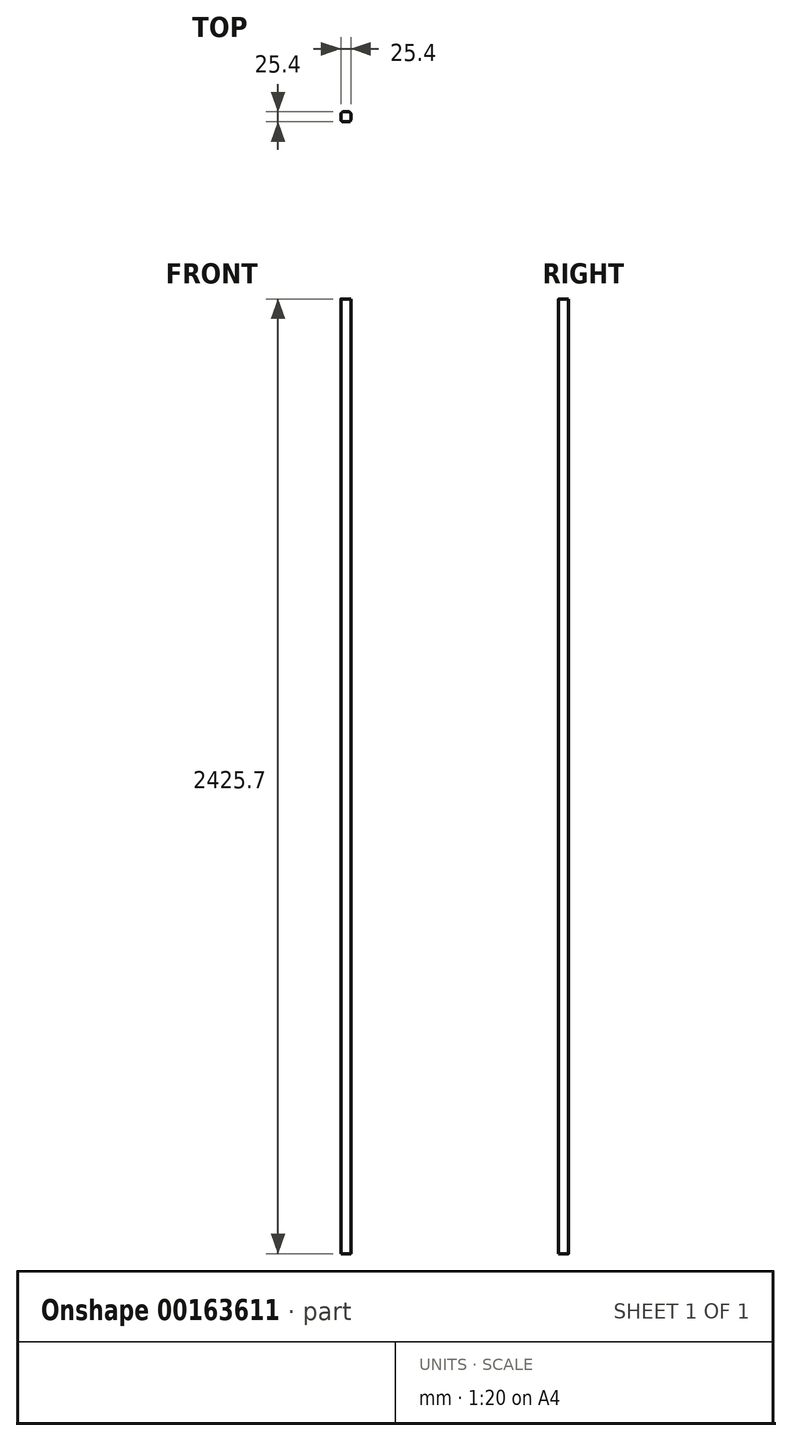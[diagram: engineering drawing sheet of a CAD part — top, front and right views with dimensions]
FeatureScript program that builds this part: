
annotation { "Feature Type Name" : "Feature", "Feature Type Description" : "" }
export const myFeature = defineFeature(function(context is Context, id is Id, definition is map)
    precondition{}
    {
        {
            var Q0;
            Q0=qCreatedBy(makeId("Top.planeOp"),FACE);
            var sketch = newSketch(context, id + "F0", { "sketchPlane" : qUnion([Q0])});
            skLineSegment(sketch, "E0.bottom", {"start": v(6.35, 12.7) * mm, "end": v(-6.35, 12.7) * mm});
            skLineSegment(sketch, "E0.top", {"start": v(6.35, -12.7) * mm, "end": v(-6.35, -12.7) * mm});
            skLineSegment(sketch, "E0.left", {"start": v(12.7, 6.35) * mm, "end": v(12.7, -6.35) * mm});
            skLineSegment(sketch, "E0.right", {"start": v(-12.7, 6.35) * mm, "end": v(-12.7, -6.35) * mm});
            skPoint(sketch, "E0.middle", {"position": v(0, 0) * mm});
            skPoint(sketch, "E1.visualSharp", {"position": v(-12.7, 12.7) * mm});
            skArc(sketch, "E1.filletArc", {"start": v(-6.35, 12.7) * mm, "mid": v(-10.84, 10.84) * mm, "end": v(-12.7, 6.35) * mm});
            skPoint(sketch, "E2.visualSharp", {"position": v(12.7, 12.7) * mm});
            skArc(sketch, "E2.filletArc", {"start": v(12.7, 6.35) * mm, "mid": v(10.84, 10.84) * mm, "end": v(6.35, 12.7) * mm});
            skPoint(sketch, "E3.visualSharp", {"position": v(12.7, -12.7) * mm});
            skArc(sketch, "E3.filletArc", {"start": v(6.35, -12.7) * mm, "mid": v(10.84, -10.84) * mm, "end": v(12.7, -6.35) * mm});
            skPoint(sketch, "E4.visualSharp", {"position": v(-12.7, -12.7) * mm});
            skArc(sketch, "E4.filletArc", {"start": v(-12.7, -6.35) * mm, "mid": v(-10.84, -10.84) * mm, "end": v(-6.35, -12.7) * mm});
            skSolve(sketch);
        }
        {
            var Q0;
            Q0 = qSketchRegion(id + "F0", true);
            extrude(context, id + "F1", {"entities" : qUnion([Q0]), "depth" : 2425.7 * mm});
        }
    });
